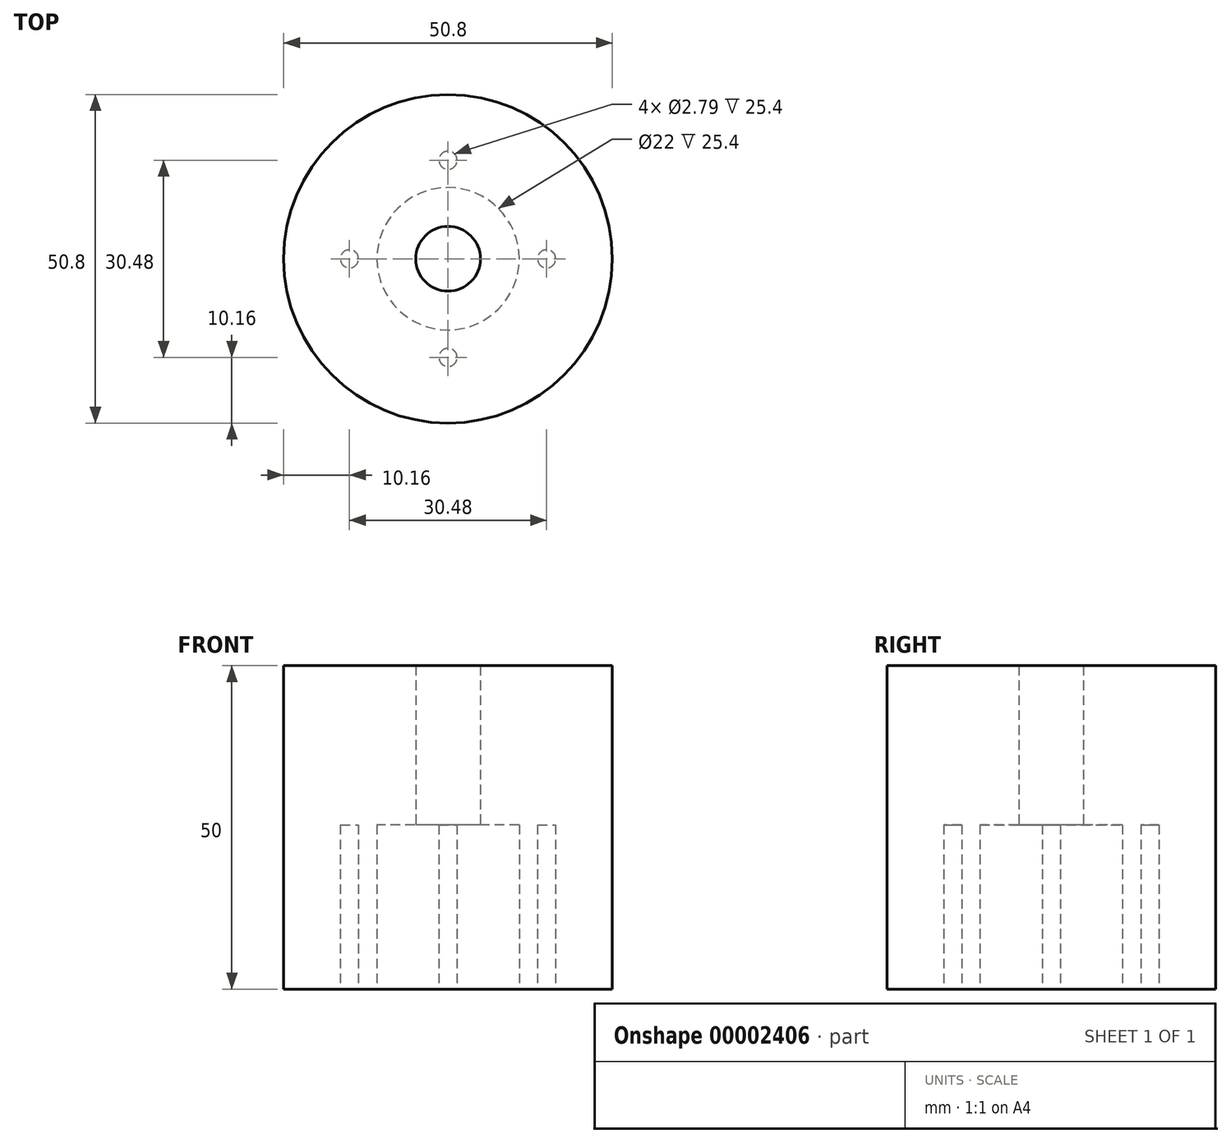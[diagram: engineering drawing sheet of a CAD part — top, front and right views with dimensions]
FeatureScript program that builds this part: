
annotation { "Feature Type Name" : "Feature", "Feature Type Description" : "" }
export const myFeature = defineFeature(function(context is Context, id is Id, definition is map)
    precondition{}
    {
        {
            var Q0;
            Q0=qCreatedBy(makeId("Top.planeOp"),FACE);
            var sketch = newSketch(context, id + "F0", { "sketchPlane" : qUnion([Q0])});
            skCircle(sketch, "E0", {"center": v(0, 0) * mm, "radius": 11 * mm});
            skCircle(sketch, "E1", {"center": v(0, 0) * mm, "radius": 25.4 * mm});
            skCircle(sketch, "E2", {"center": v(0, 0) * mm, "radius": 5 * mm});
            skSolve(sketch);
        }
        {
            var Q0;
            Q0=qSketchRegion(id+"F0",true);
            var Q1;
            Q1=makeQuery(id+"F0.imprint","IMPRINT",FACE,{"disambiguationData":[TD([[makeQuery(id+"F0.imprint","IMPRINT",EDGE,{"derivedFrom":sQuery(id+"F0.wireOp",EDGE,"E0")}),1.0]])]});
            extrude(context, id + "F1", {"entities" : qUnion([Q0, Q1]), "depth" : 50 * mm});
        }
        {
            var Q0;
            Q0=makeQuery(id+"F0.imprint","IMPRINT",FACE,{"disambiguationData":[TD([[makeQuery(id+"F0.imprint","IMPRINT",EDGE,{"derivedFrom":sQuery(id+"F0.wireOp",EDGE,"E0")}),1.0]])]});
            extrude(context, id + "F2", {"entities" : qUnion([Q0]), "operationType" : NewBodyOperationType.REMOVE, "depth" : 25.4 * mm});
        }
        {
            var Q0;
            Q0=makeQuery(id+"F1.opExtrude","CAP_FACE",FACE,{"disambiguationData":[OSD([sQuery(id+"F0.wireOp",EDGE,"E1"),sQuery(id+"F0.wireOp",EDGE,"E2")])],"isStart":true});
            var sketch = newSketch(context, id + "F3", { "sketchPlane" : qUnion([Q0])});
            skSolve(sketch);
        }
        {
            var Q0;
            Q0=makeQuery(id+"F3.imprint","IMPRINT",FACE,{"disambiguationData":[TD([[makeQuery(id+"F3.imprint","IMPRINT",EDGE,{"derivedFrom":makeQuery(id+"F1.opExtrude","CAP_EDGE",EDGE,{"disambiguationData":[OSD([sQuery(id+"F0.wireOp",EDGE,"E1")])],"isStart":true})}),-1.0]])]});
            var sketch = newSketch(context, id + "F4", { "sketchPlane" : qUnion([Q0])});
            skCircle(sketch, "E3", {"center": v(0, 15.24) * mm, "radius": 1.4 * mm});
            skCircle(sketch, "E4", {"center": v(15.24, 0) * mm, "radius": 1.4 * mm});
            skCircle(sketch, "E5", {"center": v(0, -15.24) * mm, "radius": 1.4 * mm});
            skCircle(sketch, "E6", {"center": v(-15.24, 0) * mm, "radius": 1.4 * mm});
            skSolve(sketch);
        }
        {
            var Q0;
            Q0=qSketchRegion(id+"F4",true);
            extrude(context, id + "F5", {"entities" : qUnion([Q0]), "operationType" : NewBodyOperationType.REMOVE, "oppositeDirection" : true, "depth" : 25.4 * mm});
        }
    });
